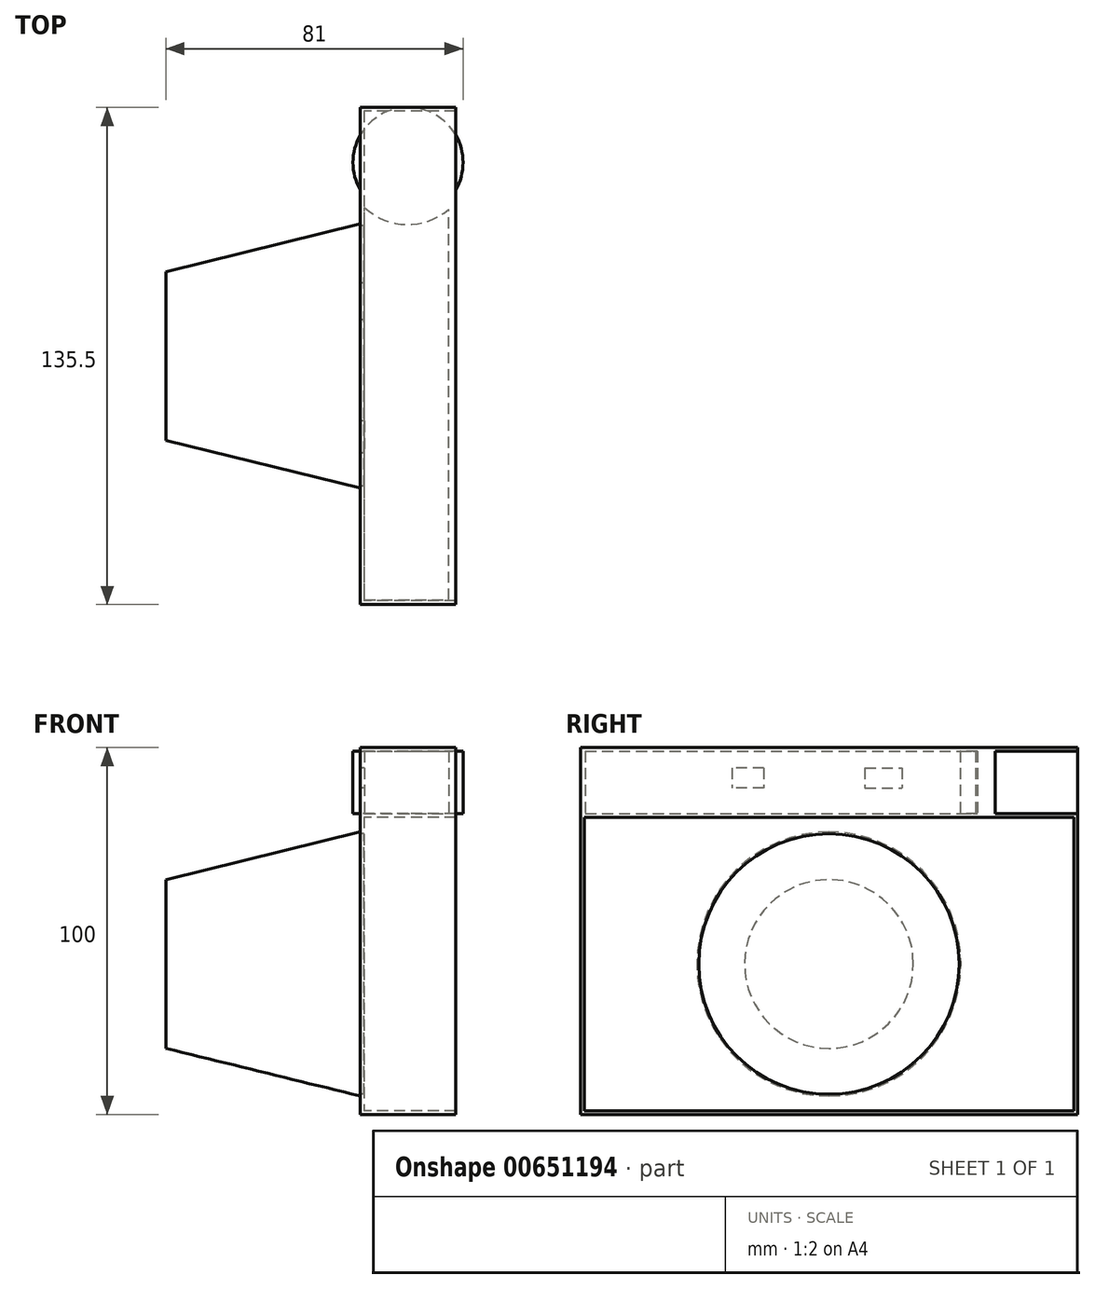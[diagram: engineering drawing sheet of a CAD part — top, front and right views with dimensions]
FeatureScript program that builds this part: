
annotation { "Feature Type Name" : "Feature", "Feature Type Description" : "" }
export const myFeature = defineFeature(function(context is Context, id is Id, definition is map)
    precondition{}
    {
        {
            var Q0;
            Q0=qCreatedBy(makeId("Right.planeOp"),FACE);
            var sketch = newSketch(context, id + "F0", { "sketchPlane" : qUnion([Q0])});
            skLineSegment(sketch, "E0.bottom", {"start": v(-67.75, 41) * mm, "end": v(67.75, 41) * mm});
            skLineSegment(sketch, "E0.top", {"start": v(-67.75, -41) * mm, "end": v(67.75, -41) * mm});
            skLineSegment(sketch, "E0.left", {"start": v(-67.75, 41) * mm, "end": v(-67.75, -41) * mm});
            skLineSegment(sketch, "E0.right", {"start": v(67.75, 41) * mm, "end": v(67.75, -41) * mm});
            skPoint(sketch, "E0.middle", {"position": v(0, 0) * mm});
            skCircle(sketch, "E1", {"center": v(0, 0) * mm, "radius": 35.5 * mm});
            skSolve(sketch);
        }
        {
            var Q0;
            Q0=qSketchRegion(id+"F0",true);
            extrude(context, id + "F1", {"entities" : qUnion([Q0]), "depth" : 1 * mm, "offsetDistance" : 25 * mm});
        }
        {
            var Q0;
            Q0=makeQuery(id+"F1.opExtrude","CAP_FACE",FACE,{"disambiguationData":[OSD([sQuery(id+"F0.wireOp",EDGE,"E0.bottom"),sQuery(id+"F0.wireOp",EDGE,"E0.top"),sQuery(id+"F0.wireOp",EDGE,"E0.left"),sQuery(id+"F0.wireOp",EDGE,"E0.right")])],"isStart":true});
            var sketch = newSketch(context, id + "F2", { "sketchPlane" : qUnion([Q0])});
            skCircle(sketch, "E2", {"center": v(0, 0) * mm, "radius": 36 * mm});
            skSolve(sketch);
        }
        {
            var Q0;
            Q0=qCreatedBy(makeId("Right.planeOp"),FACE);
            cPlane(context, id + "F3", {"entities" : qUnion([Q0]), "cplaneType" : CPlaneType.OFFSET, "offset" : 53 * mm, "oppositeDirection" : true, "width" : 150 * mm, "height" : 150 * mm});
        }
        {
            var Q0;
            Q0=qCreatedBy(id+"F3.planeOp",FACE);
            var sketch = newSketch(context, id + "F4", { "sketchPlane" : qUnion([Q0])});
            skCircle(sketch, "E3", {"center": v(0, 0) * mm, "radius": 23 * mm});
            skSolve(sketch);
        }
        {
            var Q1;
            Q1=qSketchRegion(id+"F2",true);
            var Q2;
            Q2=qSketchRegion(id+"F4",true);
            loft(context, id + "F5", {"operationType" : NewBodyOperationType.ADD, "sheetProfilesArray" : [{ "sheetProfileEntities" : qUnion([Q1]) }, { "sheetProfileEntities" : qUnion([Q2]) }]});
        }
        {
            var Q0;
            Q0=makeQuery(id+"F1.opExtrude","CAP_FACE",FACE,{"disambiguationData":[OSD([sQuery(id+"F0.wireOp",EDGE,"E0.bottom"),sQuery(id+"F0.wireOp",EDGE,"E0.top"),sQuery(id+"F0.wireOp",EDGE,"E0.left"),sQuery(id+"F0.wireOp",EDGE,"E0.right"),sQuery(id+"F0.wireOp",EDGE,"E1")])],"isStart":false});
            var sketch = newSketch(context, id + "F6", { "sketchPlane" : qUnion([Q0])});
            skLineSegment(sketch, "E4.bottom", {"start": v(67.75, 41) * mm, "end": v(-67.75, 41) * mm});
            skLineSegment(sketch, "E4.top", {"start": v(67.75, -41) * mm, "end": v(-67.75, -41) * mm});
            skLineSegment(sketch, "E4.left", {"start": v(67.75, 41) * mm, "end": v(67.75, -41) * mm});
            skLineSegment(sketch, "E4.right", {"start": v(-67.75, 41) * mm, "end": v(-67.75, -41) * mm});
            skPoint(sketch, "E4.middle", {"position": v(0, 0) * mm});
            skLineSegment(sketch, "E5.bottom", {"start": v(66.75, 40) * mm, "end": v(-66.75, 40) * mm});
            skLineSegment(sketch, "E5.top", {"start": v(66.75, -40) * mm, "end": v(-66.75, -40) * mm});
            skLineSegment(sketch, "E5.left", {"start": v(66.75, 40) * mm, "end": v(66.75, -40) * mm});
            skLineSegment(sketch, "E5.right", {"start": v(-66.75, 40) * mm, "end": v(-66.75, -40) * mm});
            skSolve(sketch);
        }
        {
            var Q0;
            Q0 = qSketchRegion(id + "F6", true);
            extrude(context, id + "F7", {"entities" : qUnion([Q0]), "operationType" : NewBodyOperationType.ADD, "depth" : 25 * mm, "offsetDistance" : 25 * mm});
        }
        {
            var Q0;
            Q0=makeQuery(id+"F7.boolean.opBoolean","MERGE",FACE,{"derivedFrom":[makeQuery(id+"F1.opExtrude","SWEPT_FACE",FACE,{"disambiguationData":[OSD([sQuery(id+"F0.wireOp",EDGE,"E0.bottom")])]}),makeQuery(id+"F7.opExtrude","SWEPT_FACE",FACE,{"disambiguationData":[OSD([sQuery(id+"F6.wireOp",EDGE,"E4.bottom")])]})]});
            var sketch = newSketch(context, id + "F8", { "sketchPlane" : qUnion([Q0])});
            skPoint(sketch, "E6.oppositeSnap0", {"position": v(13, 67.75) * mm});
            skLineSegment(sketch, "E6.bottom", {"start": v(26, 67.75) * mm, "end": v(13, 67.75) * mm, "construction": true});
            skLineSegment(sketch, "E6.top", {"start": v(26, 52.75) * mm, "end": v(13, 52.75) * mm, "construction": true});
            skLineSegment(sketch, "E6.left", {"start": v(26, 67.75) * mm, "end": v(26, 52.75) * mm, "construction": true});
            skLineSegment(sketch, "E6.right", {"start": v(13, 67.75) * mm, "end": v(13, 52.75) * mm, "construction": true});
            skCircle(sketch, "E7", {"center": v(13, 52.75) * mm, "radius": 15 * mm});
            skSolve(sketch);
        }
        {
            var Q0;
            Q0 = qSketchRegion(id + "F8", true);
            extrude(context, id + "F9", {"entities" : qUnion([Q0]), "operationType" : NewBodyOperationType.ADD, "depth" : 17 * mm, "offsetDistance" : 25 * mm});
        }
        {
            var Q0;
            {var subQ0=sQuery(id+"F6.wireOp",EDGE,"E4.right");var subQ1=sQuery(id+"F0.wireOp",EDGE,"E0.left");var subQ2=sQuery(id+"F0.wireOp",EDGE,"E0.bottom");var subQ3=sQuery(id+"F8.wireOp",EDGE,"E7");var subQ4=sQuery(id+"F6.wireOp",EDGE,"E4.bottom");Q0=makeQuery(id+"F9.boolean.opBoolean","SPLIT",FACE,{"disambiguationData":[TD([makeQuery(id+"F1.opExtrude","CAP_FACE",FACE,{"disambiguationData":[OSD([subQ2,sQuery(id+"F0.wireOp",EDGE,"E0.top"),subQ1,sQuery(id+"F0.wireOp",EDGE,"E0.right"),sQuery(id+"F0.wireOp",EDGE,"E1")])],"isStart":true}),makeQuery(id+"F1.opExtrude","SWEPT_FACE",FACE,{"disambiguationData":[OSD([subQ1])]}),makeQuery(id+"F7.opExtrude","CAP_FACE",FACE,{"disambiguationData":[OSD([subQ4,sQuery(id+"F6.wireOp",EDGE,"E4.top"),sQuery(id+"F6.wireOp",EDGE,"E4.left"),subQ0,sQuery(id+"F6.wireOp",EDGE,"E5.bottom"),sQuery(id+"F6.wireOp",EDGE,"E5.top"),sQuery(id+"F6.wireOp",EDGE,"E5.left"),sQuery(id+"F6.wireOp",EDGE,"E5.right")])],"isStart":false}),makeQuery(id+"F7.opExtrude","SWEPT_FACE",FACE,{"disambiguationData":[OSD([subQ0])]}),makeQuery(id+"F9.opExtrude","SWEPT_FACE",FACE,{"disambiguationData":[OSD([subQ3])]}),makeQuery(id+"F9.opExtrude","CAP_FACE",FACE,{"disambiguationData":[OSD([subQ3])],"isStart":true})])],"derivedFrom":makeQuery(id+"F7.boolean.opBoolean","MERGE",FACE,{"derivedFrom":[makeQuery(id+"F1.opExtrude","SWEPT_FACE",FACE,{"disambiguationData":[OSD([subQ2])]}),makeQuery(id+"F7.opExtrude","SWEPT_FACE",FACE,{"disambiguationData":[OSD([subQ4])]})]})});}
            var sketch = newSketch(context, id + "F10", { "sketchPlane" : qUnion([Q0])});
            skLineSegment(sketch, "E8", {"start": v(26, -67.75) * mm, "end": v(0, -67.75) * mm});
            skLineSegment(sketch, "E9", {"start": v(0, -67.75) * mm, "end": v(0, 45.27) * mm});
            skLineSegment(sketch, "E10", {"start": v(26, -67.75) * mm, "end": v(26, 45.27) * mm});
            skArc(sketch, "E11", {"start": v(0, 45.27) * mm, "mid": v(13, 37.77) * mm, "end": v(26, 45.27) * mm});
            skLineSegment(sketch, "E12", {"start": v(1.18, -66.4) * mm, "end": v(24.07, -66.4) * mm});
            skLineSegment(sketch, "E13", {"start": v(24.07, -66.4) * mm, "end": v(24.07, 40) * mm});
            skLineSegment(sketch, "E14", {"start": v(1.18, -66.4) * mm, "end": v(1.18, 40.5) * mm});
            skArc(sketch, "E15", {"start": v(1.18, 40.5) * mm, "mid": v(12.52, 35.81) * mm, "end": v(24.07, 40) * mm});
            skSolve(sketch);
        }
        {
            var Q0;
            Q0 = qSketchRegion(id + "F10", true);
            extrude(context, id + "F11", {"entities" : qUnion([Q0]), "operationType" : NewBodyOperationType.ADD, "depth" : 17 * mm, "offsetDistance" : 25 * mm});
        }
        {
            var Q0;
            Q0=makeQuery(id+"F11.boolean.opBoolean","MERGE",FACE,{"derivedFrom":[makeQuery(id+"F9.opExtrude","CAP_FACE",FACE,{"disambiguationData":[OSD([sQuery(id+"F8.wireOp",EDGE,"E7")])],"isStart":false}),makeQuery(id+"F11.opExtrude","CAP_FACE",FACE,{"disambiguationData":[OSD([sQuery(id+"F10.wireOp",EDGE,"E8"),sQuery(id+"F10.wireOp",EDGE,"E9"),sQuery(id+"F10.wireOp",EDGE,"E10"),sQuery(id+"F10.wireOp",EDGE,"E11"),sQuery(id+"F10.wireOp",EDGE,"E12"),sQuery(id+"F10.wireOp",EDGE,"E13"),sQuery(id+"F10.wireOp",EDGE,"E14"),sQuery(id+"F10.wireOp",EDGE,"E15")])],"isStart":false})]});
            var sketch = newSketch(context, id + "F12", { "sketchPlane" : qUnion([Q0])});
            skLineSegment(sketch, "E16.bottom", {"start": v(0, -67.75) * mm, "end": v(26, -67.75) * mm});
            skLineSegment(sketch, "E16.top", {"start": v(0, 67.75) * mm, "end": v(26, 67.75) * mm});
            skLineSegment(sketch, "E16.left", {"start": v(0, -67.75) * mm, "end": v(0, 67.75) * mm});
            skLineSegment(sketch, "E16.right", {"start": v(26, -67.75) * mm, "end": v(26, 67.75) * mm});
            skSolve(sketch);
        }
        {
            var Q0;
            Q0 = qSketchRegion(id + "F12", true);
            extrude(context, id + "F13", {"entities" : qUnion([Q0]), "operationType" : NewBodyOperationType.ADD, "depth" : 1 * mm, "offsetDistance" : 25 * mm});
        }
        {
            var Q0;
            Q0=makeQuery(id+"F13.boolean.opBoolean","MERGE",FACE,{"derivedFrom":[makeQuery(id+"F11.boolean.opBoolean","MERGE",FACE,{"derivedFrom":[makeQuery(id+"F1.opExtrude","CAP_FACE",FACE,{"disambiguationData":[OSD([sQuery(id+"F0.wireOp",EDGE,"E0.bottom"),sQuery(id+"F0.wireOp",EDGE,"E0.top"),sQuery(id+"F0.wireOp",EDGE,"E0.left"),sQuery(id+"F0.wireOp",EDGE,"E0.right"),sQuery(id+"F0.wireOp",EDGE,"E1")])],"isStart":true}),makeQuery(id+"F11.opExtrude","SWEPT_FACE",FACE,{"disambiguationData":[OSD([sQuery(id+"F10.wireOp",EDGE,"E9")])]})]}),makeQuery(id+"F13.opExtrude","SWEPT_FACE",FACE,{"disambiguationData":[OSD([sQuery(id+"F12.wireOp",EDGE,"E16.left")])]})]});
            var sketch = newSketch(context, id + "F14", { "sketchPlane" : qUnion([Q0])});
            skLineSegment(sketch, "E17.bottom", {"start": v(17.74, 53.41) * mm, "end": v(26.41, 53.41) * mm});
            skLineSegment(sketch, "E17.top", {"start": v(17.74, 48) * mm, "end": v(26.41, 48) * mm});
            skLineSegment(sketch, "E17.left", {"start": v(17.74, 53.41) * mm, "end": v(17.74, 48) * mm});
            skLineSegment(sketch, "E17.right", {"start": v(26.41, 53.41) * mm, "end": v(26.41, 48) * mm});
            skLineSegment(sketch, "E18.bottom", {"start": v(-9.8, 53.41) * mm, "end": v(-19.87, 53.41) * mm});
            skLineSegment(sketch, "E18.top", {"start": v(-9.8, 48) * mm, "end": v(-19.87, 48) * mm});
            skLineSegment(sketch, "E18.left", {"start": v(-9.8, 53.41) * mm, "end": v(-9.8, 48) * mm});
            skLineSegment(sketch, "E18.right", {"start": v(-19.87, 53.41) * mm, "end": v(-19.87, 48) * mm});
            skSolve(sketch);
        }
        {
            var Q0;
            Q0 = qSketchRegion(id + "F14", true);
            extrude(context, id + "F15", {"entities" : qUnion([Q0]), "operationType" : NewBodyOperationType.REMOVE, "oppositeDirection" : true, "depth" : 17.4 * mm, "offsetDistance" : 25 * mm});
        }
    });
